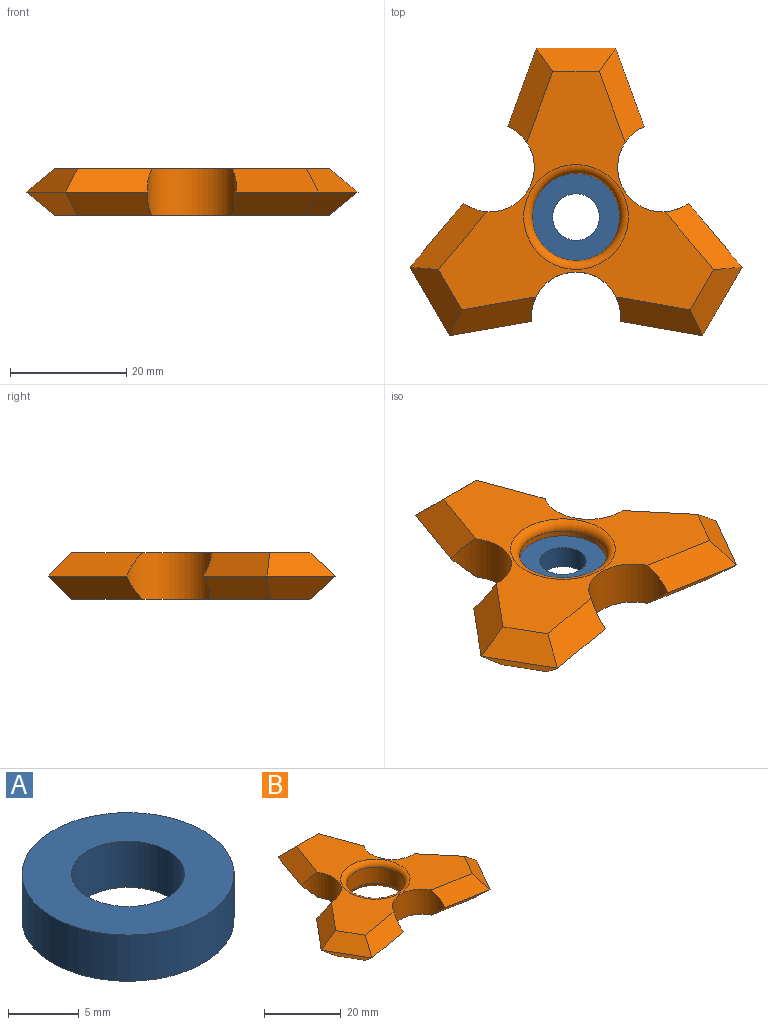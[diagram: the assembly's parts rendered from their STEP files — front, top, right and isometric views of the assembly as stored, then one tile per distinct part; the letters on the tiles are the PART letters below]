
ASSEMBLY  parts=2 mates=1
PART A: 4 faces, bbox 15x15x4 mm
  f0: cylinder r=4mm len=8mm, axis (0,0,-1), area 100.5mm2, adj f2,f3
  f1: cylinder r=7.5mm len=15mm, axis (0,0,-1), area 188.5mm2, adj f2,f3
  f2: plane 15x15mm, normal (0,0,1), area 126.4mm2, adj f0,f1
  f3: plane 15x15mm, normal (0,0,-1), area 126.4mm2, adj f0,f1
PART B: 26 faces, bbox 57x49.4x8 mm
  f0: cylinder r=7.67mm len=14.67mm, axis (0,0,-1), area 172mm2, adj f3,f4,f16,f17,f20,f21
  f1: cylinder r=7.67mm len=14.67mm, axis (0,0,-1), area 172mm2, adj f3,f4,f14,f15,f24,f25
  f2: cylinder r=7.67mm len=15.34mm, axis (0,0,-1), area 172mm2, adj f3,f4,f18,f19,f22,f23
  f3: plane 47.3x40.96mm, normal (0,0,1), area 681.4mm2, adj f0,f1,f2,f6,f8,f10,f12,f14
  f4: plane 47.3x40.96mm, normal (0,0,-1), area 681.4mm2, adj f0,f1,f2,f7,f9,f11,f13,f15
  f5: cylinder r=7.5mm len=15mm, axis (0,0,1), area 235.6mm2, adj f12,f13
  f6: plane 11.78x8.86mm, normal (0.61,-0.35,0.71), area 61.1mm2, adj f3,f7,f19,f21
  f7: plane 11.78x8.86mm, normal (0.61,-0.35,-0.71), area 61.1mm2, adj f4,f6,f18,f20
  f8: plane 11.78x8.86mm, normal (-0.61,-0.35,0.71), area 61.1mm2, adj f3,f9,f22,f24
  f9: plane 11.78x8.86mm, normal (-0.61,-0.35,-0.71), area 61.1mm2, adj f4,f8,f23,f25
  f10: plane 13.6x4mm, normal (0,0.71,0.71), area 61.1mm2, adj f3,f11,f14,f16
  f11: plane 13.6x4mm, normal (0,0.71,-0.71), area 61.1mm2, adj f4,f10,f15,f17
  f12: torus R=9mm, axis (0,0,1), area 119.1mm2, adj f3,f5
  f13: torus R=9mm, axis (0,0,1), area 119.1mm2, adj f4,f5
  f14: plane 16.19x7.69mm, normal (-0.66,0.24,0.71), area 75.9mm2, adj f1,f3,f10,f15
  f15: plane 16.19x7.69mm, normal (-0.66,0.24,-0.71), area 75.9mm2, adj f1,f4,f11,f14
  f16: plane 16.19x7.69mm, normal (0.66,0.24,0.71), area 75.9mm2, adj f0,f3,f10,f17
  f17: plane 16.19x7.69mm, normal (0.66,0.24,-0.71), area 75.9mm2, adj f0,f4,f11,f16
  f18: plane 14.84x6.68mm, normal (-0.12,-0.7,-0.71), area 75.9mm2, adj f2,f4,f7,f19
  f19: plane 14.84x6.68mm, normal (-0.12,-0.7,0.71), area 75.9mm2, adj f2,f3,f6,f18
  f20: plane 13.21x11.38mm, normal (0.54,0.45,-0.71), area 75.9mm2, adj f0,f4,f7,f21
  f21: plane 13.21x11.38mm, normal (0.54,0.45,0.71), area 75.9mm2, adj f0,f3,f6,f20
  f22: plane 14.84x6.68mm, normal (0.12,-0.7,0.71), area 75.9mm2, adj f2,f3,f8,f23
  f23: plane 14.84x6.68mm, normal (0.12,-0.7,-0.71), area 75.9mm2, adj f2,f4,f9,f22
  f24: plane 13.21x11.38mm, normal (-0.54,0.45,0.71), area 75.9mm2, adj f1,f3,f8,f25
  f25: plane 13.21x11.38mm, normal (-0.54,0.45,-0.71), area 75.9mm2, adj f1,f4,f9,f24
PLACE A t=(42.67,12.99,-22.82)mm
PLACE B t=(42.67,12.99,-22.32)mm
MATE revolute B.f5 <-> A.f0  axis (0,0,1) through (42.67,12.99,-20.82)mm
